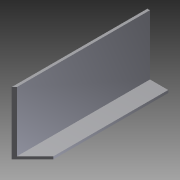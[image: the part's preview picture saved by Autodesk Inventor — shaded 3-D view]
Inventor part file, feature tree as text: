
AUTODESK INVENTOR PART (.ipt)
format: ipt  version: 2012 (Build 160160000, 160)  size: 80,896 bytes
history: native  units: in
note: dims shown in document units (in); Inventor stores cm internally (conversion verified against a paired STEP export)
features: extrude x2, sketch x2
ambient origin geometry x8: Origin, YZ Plane, XZ Plane, XY Plane, X Axis, Y Axis, Z Axis, Center Point
bodies: Solid1 (feature_tree)
feature tree (4):
  extrude  "Extrusion1"  Depth=3.0in
  extrude  "Extrusion2"  Depth=6.5in TaperAngle=0.0deg
  sketch  "Sketch1"  dims[d0=0.125in d1=3.0in]
  sketch  "Sketch2"  dims[d2=1.0in d3=6.5in d4=0.0in d5=45.0deg d6=6.5in d7=0.0in]
